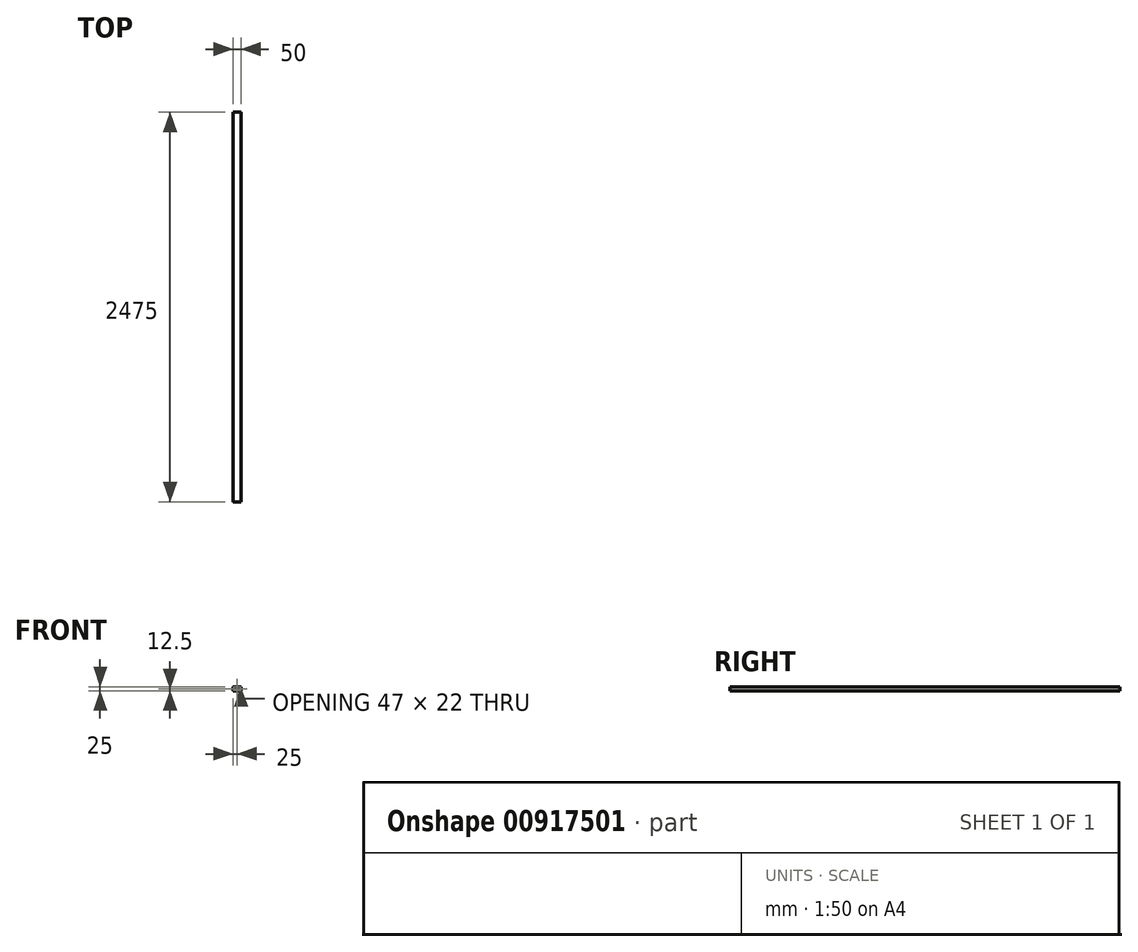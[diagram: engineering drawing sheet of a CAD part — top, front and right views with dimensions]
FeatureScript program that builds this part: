
annotation { "Feature Type Name" : "Feature", "Feature Type Description" : "" }
export const myFeature = defineFeature(function(context is Context, id is Id, definition is map)
    precondition{}
    {
        {
            var Q0;
            Q0=qCreatedBy(makeId("Front.planeOp"),FACE);
            var sketch = newSketch(context, id + "F0", { "sketchPlane" : qUnion([Q0])});
            skLineSegment(sketch, "E0.bottom", {"start": v(22.5, 12.5) * mm, "end": v(-22.5, 12.5) * mm});
            skLineSegment(sketch, "E0.top", {"start": v(22.5, -12.5) * mm, "end": v(-22.5, -12.5) * mm});
            skLineSegment(sketch, "E0.left", {"start": v(25, 10) * mm, "end": v(25, -10) * mm});
            skLineSegment(sketch, "E0.right", {"start": v(-25, 10) * mm, "end": v(-25, -10) * mm});
            skPoint(sketch, "E0.middle", {"position": v(0, 0) * mm});
            skPoint(sketch, "E1.visualSharp", {"position": v(25, 12.5) * mm});
            skArc(sketch, "E1.filletArc", {"start": v(25, 10) * mm, "mid": v(24.27, 11.77) * mm, "end": v(22.5, 12.5) * mm});
            skPoint(sketch, "E2.visualSharp", {"position": v(25, -12.5) * mm});
            skArc(sketch, "E2.filletArc", {"start": v(22.5, -12.5) * mm, "mid": v(24.27, -11.77) * mm, "end": v(25, -10) * mm});
            skPoint(sketch, "E3.visualSharp", {"position": v(-25, -12.5) * mm});
            skArc(sketch, "E3.filletArc", {"start": v(-25, -10) * mm, "mid": v(-24.27, -11.77) * mm, "end": v(-22.5, -12.5) * mm});
            skPoint(sketch, "E4.visualSharp", {"position": v(-25, 12.5) * mm});
            skArc(sketch, "E4.filletArc", {"start": v(-22.5, 12.5) * mm, "mid": v(-24.27, 11.77) * mm, "end": v(-25, 10) * mm});
            skLineSegment(sketch, "E5.0", {"start": v(23.5, 10) * mm, "end": v(23.5, -10) * mm});
            skLineSegment(sketch, "E5.1", {"start": v(22.5, 11) * mm, "end": v(-22.5, 11) * mm});
            skLineSegment(sketch, "E5.2", {"start": v(-23.5, 10) * mm, "end": v(-23.5, -10) * mm});
            skLineSegment(sketch, "E5.3", {"start": v(22.5, -11) * mm, "end": v(-22.5, -11) * mm});
            skPoint(sketch, "E6.visualSharp", {"position": v(-23.5, 11) * mm});
            skArc(sketch, "E6.filletArc", {"start": v(-22.5, 11) * mm, "mid": v(-23.2, 10.7) * mm, "end": v(-23.5, 10) * mm});
            skPoint(sketch, "E7.visualSharp", {"position": v(-23.5, -11) * mm});
            skArc(sketch, "E7.filletArc", {"start": v(-23.5, -10) * mm, "mid": v(-23.2, -10.7) * mm, "end": v(-22.5, -11) * mm});
            skPoint(sketch, "E8.visualSharp", {"position": v(23.5, -11) * mm});
            skArc(sketch, "E8.filletArc", {"start": v(22.5, -11) * mm, "mid": v(23.2, -10.7) * mm, "end": v(23.5, -10) * mm});
            skPoint(sketch, "E9.visualSharp", {"position": v(23.5, 11) * mm});
            skArc(sketch, "E9.filletArc", {"start": v(23.5, 10) * mm, "mid": v(23.2, 10.7) * mm, "end": v(22.5, 11) * mm});
            skSolve(sketch);
        }
        {
            var Q0;
            Q0 = qSketchRegion(id + "F0", true);
            extrude(context, id + "F1", {"entities" : qUnion([Q0]), "depth" : 2475 * mm, "offsetDistance" : 25 * mm, "symmetric" : true});
        }
    });
